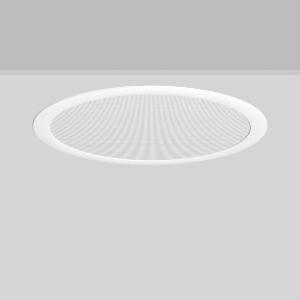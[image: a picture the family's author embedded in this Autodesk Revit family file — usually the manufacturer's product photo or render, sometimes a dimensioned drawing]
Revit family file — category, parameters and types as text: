
# Revit family: toledo_flat_pro_e_901719_002_1_76_8db8
name_source: partatom
category: Lighting Fixtures
units: mm (PartAtom-declared; Revit-internal decimal feet)

## family parameters
Cut with Voids When Loaded = No
Host = Face
Light Source = No
Part Type = Normal
Room Calculation Point = No
Round Connector Dimension = Use Diameter
Shared = No

## types (1)
- TOLEDO FLAT pro E (1 x LED Modul 940, 2800 lm, 4000)
    Apparent Load = 26 VA
    CIE Flux Codes = 66 90 98 100 100
    Color Rendering = 92
    Color Temperature = 4000
    Default Elevation = 1800 mm
    Description = Series: TOLEDO FLAT pro
Super-flat recessed downlight for high requirements. Housing: die-cast aluminium. Diffuser made from resistant polycarbonate (PC) with smooth surface on room side for low sensitivity to dirt and for the prevention of the accumulation of germs and bacteria. Satinised microprismatic diffuser prevents direct glare. Ceiling installation with spring system. Mounting depth depends on ceiling strength. Suitable for through-wiring. Including separate LED converter with connecting cable 250 mm. Cyanosis Observation Index (COI) <3.3. 
Colour: white
Diameter: 495 mm
Height: 6 mm
Cut-out diameter: 470 mm
Recess height: 35-55 mm
Luminaire: recess height: 31-51 mm
Lamp: LED
Socket: without socket
Colour temperature: 4000K
Colour rendering index (CRI): 90
System power: 26 W
Rated luminous flux: 2800 lm
Luminous efficiency: 108 lm/W
Control gear: Converter, dimmable, DALI
Protection class: II
Type of protection: IP 54
    Height = 0 mm  [stored 0 ft]
    Lamp = 1 x LED Modul 940
    Lamp Light Flux = 2800 lm
    Lamp count = 1
    Length = 495 mm
    Lifetime = 50000 h
    Luminous efficacy = 108 lm/W
    Manufacturer = RZB
    ModVariant = No
    Model = 901719.002.1.76
    Mounting Place = Ceiling
    Mounting Type = Recessed
    Number of Poles = 1
    OnlyDefault = Yes
    Power Factor = 1
    Product Name = TOLEDO FLAT pro E
    Product group = Recessed downlights
    ProductGroupID = 402
    Protection Class = Protection class II
    Protection Degree = Degree of protection
    RLX_Detail_Level = 1
    RLX_Emergency_Light_Flux = 0 lm
    RLX_Emergency_Type = 0
    RLX_Emergency_Type_DB = No
    RlxData = <blob elided: 38121 chars, md5=dbe83f27>
    Socket = socket
    Standby Power = 0 W
    System Light Flux = 2800 lm
    System Power = 26 W
    Type Comments = Product without accessories
    Type Image = 901719.002.76.jpg
    URL = http://relux.com
    VarID = ---
    Voltage = 0 V
    Weight = 0.00 kg
    Width = 0 mm  [stored 0 ft]

note: [stored X ft] marks values corroborated as IEEE doubles in the binary element streams (Revit-internal decimal feet)

## geometry (parser evidence)
native form markers: Blend x4, Sweep x10
no freeform markers — native parametric forms only
